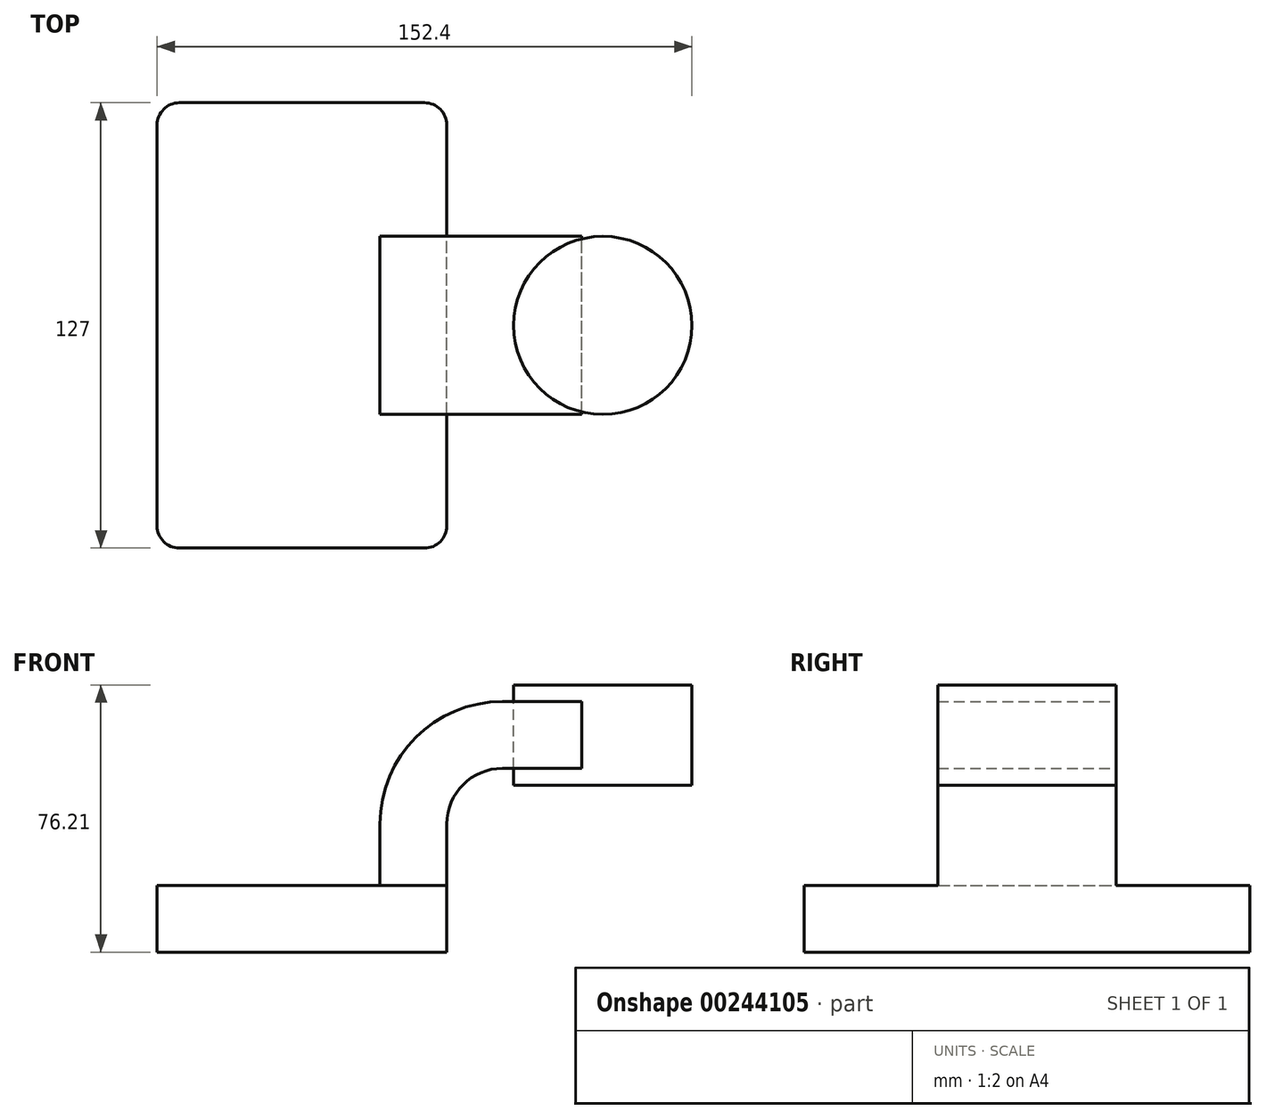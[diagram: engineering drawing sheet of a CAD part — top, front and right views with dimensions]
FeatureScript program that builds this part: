
annotation { "Feature Type Name" : "Feature", "Feature Type Description" : "" }
export const myFeature = defineFeature(function(context is Context, id is Id, definition is map)
    precondition{}
    {
        {
            var Q0;
            Q0=qCreatedBy(makeId("Front.planeOp"),FACE);
            var sketch = newSketch(context, id + "F0", { "sketchPlane" : qUnion([Q0])});
            skLineSegment(sketch, "E0.bottom", {"start": v(41.27, 9.53) * mm, "end": v(-41.28, 9.53) * mm});
            skLineSegment(sketch, "E0.top", {"start": v(41.28, -9.52) * mm, "end": v(-41.27, -9.52) * mm});
            skLineSegment(sketch, "E0.left", {"start": v(41.28, 9.53) * mm, "end": v(41.28, -9.52) * mm});
            skLineSegment(sketch, "E0.right", {"start": v(-41.28, 9.53) * mm, "end": v(-41.27, -9.52) * mm});
            skPoint(sketch, "E0.middle", {"position": v(0, 0) * mm});
            skLineSegment(sketch, "E1.bottom", {"start": v(111.12, 38.1) * mm, "end": v(60.32, 38.1) * mm});
            skLineSegment(sketch, "E1.top", {"start": v(111.12, 66.68) * mm, "end": v(60.32, 66.68) * mm});
            skLineSegment(sketch, "E1.left", {"start": v(111.12, 38.1) * mm, "end": v(111.12, 66.68) * mm});
            skLineSegment(sketch, "E1.right", {"start": v(60.32, 38.1) * mm, "end": v(60.32, 66.68) * mm});
            skPoint(sketch, "E1.middle", {"position": v(85.72, 52.39) * mm});
            skLineSegment(sketch, "E2", {"start": v(41.27, 9.53) * mm, "end": v(41.27, 27) * mm});
            skArc(sketch, "E3", {"start": v(41.27, 27) * mm, "mid": v(45.92, 38.23) * mm, "end": v(57.15, 42.88) * mm});
            skLineSegment(sketch, "E4", {"start": v(57.15, 42.88) * mm, "end": v(79.7, 42.88) * mm});
            skLineSegment(sketch, "E5.0", {"start": v(57.15, 61.93) * mm, "end": v(79.7, 61.93) * mm});
            skArc(sketch, "E5.1", {"start": v(22.23, 27) * mm, "mid": v(32.45, 51.7) * mm, "end": v(57.15, 61.93) * mm});
            skLineSegment(sketch, "E5.2", {"start": v(22.22, 9.53) * mm, "end": v(22.22, 27) * mm});
            skLineSegment(sketch, "E6", {"start": v(79.7, 42.88) * mm, "end": v(79.7, 61.93) * mm});
            skFitSpline(sketch, "E7", {"points": [v(-41.28, 9.53) * mm, v(57.15, 61.93) * mm], "startDerivative": vector(41.34, 92.13) * mm, "endDerivative": vector(126.92, -9.42) * mm});
            skLineSegment(sketch, "E8", {"start": v(85.72, 66.68) * mm, "end": v(85.72, 38.1) * mm});
            skSolve(sketch);
        }
        {
            var Q0;
            Q0=makeQuery(id+"F0.imprint","IMPRINT",FACE,{"disambiguationData":[TD([[makeQuery(id+"F0.imprint","IMPRINT",EDGE,{"derivedFrom":sQuery(id+"F0.wireOp",EDGE,"E0.top")}),-1.0]])]});
            extrude(context, id + "F1", {"entities" : qUnion([Q0]), "endBound" : BoundingType.SYMMETRIC, "depth" : 127 * mm});
        }
        {
            var Q0;
            {var subQ1=sQuery(id+"F0.wireOp",EDGE,"E2");Q0=makeQuery(id+"F0.imprint","IMPRINT",FACE,{"disambiguationData":[TD([[makeQuery(id+"F0.imprint","IMPRINT",EDGE,{"derivedFrom":subQ1}),1.0]])]});}
            var Q1;
            {var subQ5=sQuery(id+"F0.wireOp",EDGE,"E6");Q1=makeQuery(id+"F0.imprint","IMPRINT",FACE,{"disambiguationData":[TD([[makeQuery(id+"F0.imprint","IMPRINT",EDGE,{"derivedFrom":subQ5}),1.0]])]});}
            extrude(context, id + "F2", {"entities" : qUnion([Q0, Q1]), "operationType" : NewBodyOperationType.ADD, "endBound" : BoundingType.SYMMETRIC, "depth" : 50.8 * mm});
        }
        {
            var Q0;
            Q0=makeQuery(id+"F0.imprint","IMPRINT",FACE,{"disambiguationData":[TD([[makeQuery(id+"F0.imprint","IMPRINT",EDGE,{"derivedFrom":sQuery(id+"F0.wireOp",EDGE,"E5.1")}),1.0]])]});
            extrude(context, id + "F3", {"entities" : qUnion([Q0]), "operationType" : NewBodyOperationType.ADD, "endBound" : BoundingType.SYMMETRIC, "depth" : 15.88 * mm});
        }
        {
            var Q0;
            {var subQ1=sQuery(id+"F0.wireOp",EDGE,"E1.bottom");Q0=makeQuery(id+"F0.imprint","IMPRINT",FACE,{"disambiguationData":[TD([[makeQuery(id+"F0.imprint","IMPRINT",EDGE,{"derivedFrom":subQ1}),-1.0]])]});}
            var Q1;
            Q1=sQuery(id+"F0.wireOp",EDGE,"E8");
            revolve(context, id + "F4", {"entities" : qUnion([Q0]), "axis" : qUnion([Q1]), "revolveType" : RevolveType.FULL});
        }
        {
            var Q0;
            Q0=makeQuery(id+"F1.opExtrude","CAP_EDGE",EDGE,{"disambiguationData":[OSD([sQuery(id+"F0.wireOp",EDGE,"E0.left")])],"isStart":false});
            var Q1;
            Q1=makeQuery(id+"F1.opExtrude","CAP_EDGE",EDGE,{"disambiguationData":[OSD([sQuery(id+"F0.wireOp",EDGE,"E0.right")])],"isStart":false});
            var Q2;
            Q2=makeQuery(id+"F1.opExtrude","CAP_EDGE",EDGE,{"disambiguationData":[OSD([sQuery(id+"F0.wireOp",EDGE,"E0.left")])],"isStart":true});
            var Q3;
            Q3=makeQuery(id+"F1.opExtrude","CAP_EDGE",EDGE,{"disambiguationData":[OSD([sQuery(id+"F0.wireOp",EDGE,"E0.right")])],"isStart":true});
            fillet(context, id + "F5", {"entities" : qUnion([Q0, Q1, Q2, Q3]), "radius" : 6.35 * mm, "tangentPropagation" : true, "allowEdgeOverflow" : false});
        }
    });
